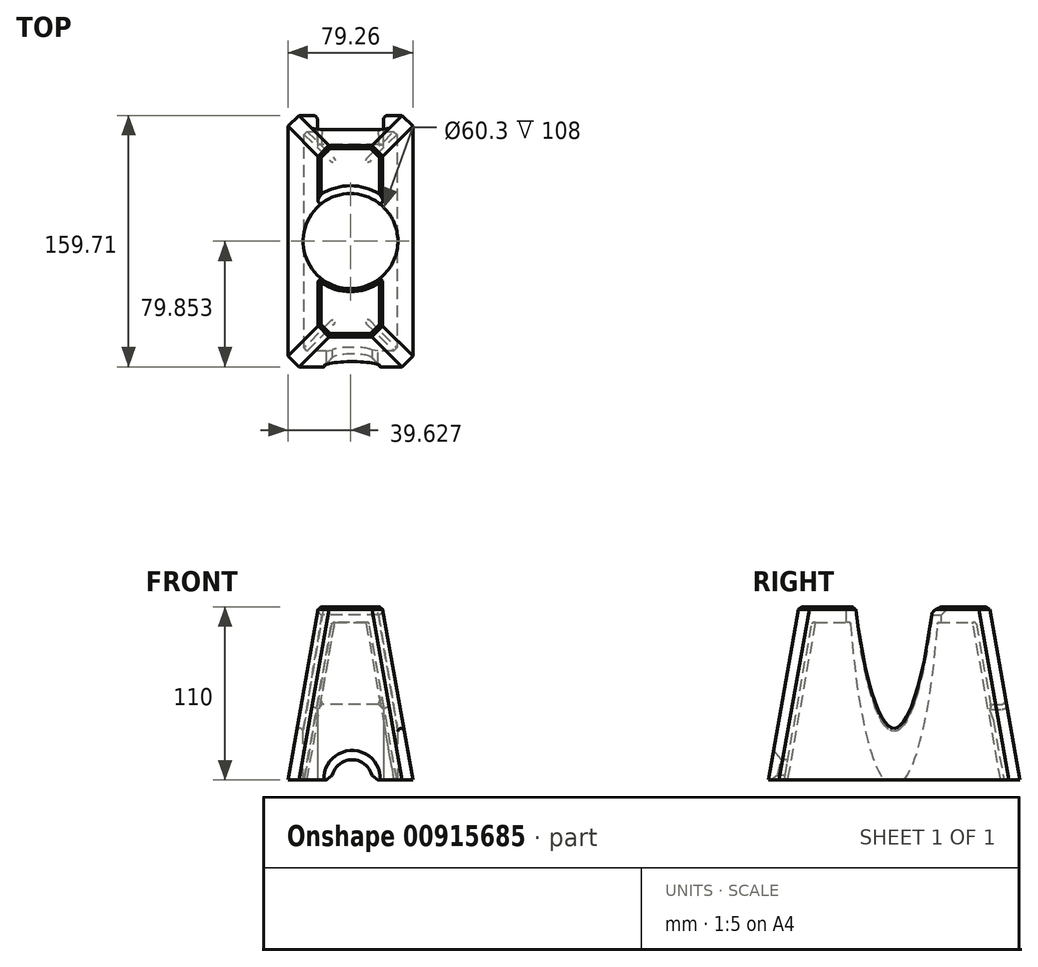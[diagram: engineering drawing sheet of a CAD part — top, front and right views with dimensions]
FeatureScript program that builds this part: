
annotation { "Feature Type Name" : "Feature", "Feature Type Description" : "" }
export const myFeature = defineFeature(function(context is Context, id is Id, definition is map)
    precondition{}
    {
        {
            var Q0;
            Q0=qCreatedBy(makeId("Top.planeOp"),FACE);
            var sketch = newSketch(context, id + "F0", { "sketchPlane" : qUnion([Q0])});
            skLineSegment(sketch, "E0.bottom", {"start": v(58.95, 0) * mm, "end": v(0, 0) * mm});
            skLineSegment(sketch, "E0.top", {"start": v(58.95, 139.4) * mm, "end": v(0, 139.4) * mm});
            skLineSegment(sketch, "E0.left", {"start": v(58.95, 0) * mm, "end": v(58.95, 139.4) * mm});
            skLineSegment(sketch, "E0.right", {"start": v(0, 0) * mm, "end": v(0, 139.4) * mm});
            skSolve(sketch);
        }
        {
            var Q0;
            Q0=makeQuery(id+"F0.imprint","IMPRINT",FACE,{"disambiguationData":[TD([[makeQuery(id+"F0.imprint","IMPRINT",EDGE,{"derivedFrom":sQuery(id+"F0.wireOp",EDGE,"E0.bottom")}),-1.0]])]});
            extrude(context, id + "F1", {"entities" : qUnion([Q0]), "depth" : 100 * mm, "offsetDistance" : 25 * mm, "hasDraft" : true, "draftAngle" : 10 * degree, "draftPullDirection" : true});
        }
        {
            var Q0;
            Q0=makeQuery(id+"F1.opExtrude","CAP_FACE",FACE,{"disambiguationData":[OSD([sQuery(id+"F0.wireOp",EDGE,"E0.bottom"),sQuery(id+"F0.wireOp",EDGE,"E0.top"),sQuery(id+"F0.wireOp",EDGE,"E0.left"),sQuery(id+"F0.wireOp",EDGE,"E0.right")])],"isStart":true});
            shell(context, id + "F2", {"entities" : qUnion([Q0]), "thickness" : 10 * mm, "oppositeDirection" : true});
        }
        {
            var Q0;
            Q0=makeQuery(id+"F1.opExtrude","CAP_FACE",FACE,{"disambiguationData":[OSD([sQuery(id+"F0.wireOp",EDGE,"E0.bottom"),sQuery(id+"F0.wireOp",EDGE,"E0.top"),sQuery(id+"F0.wireOp",EDGE,"E0.left"),sQuery(id+"F0.wireOp",EDGE,"E0.right")])],"isStart":false});
            var sketch = newSketch(context, id + "F3", { "sketchPlane" : qUnion([Q0])});
            skLineSegment(sketch, "E1", {"start": v(29.48, 130.16) * mm, "end": v(29.48, 9.24) * mm});
            skCircle(sketch, "E2", {"center": v(29.48, 69.7) * mm, "radius": 30.15 * mm});
            skSolve(sketch);
        }
        {
            var Q0;
            {var subQ0=sQuery(id+"F3.wireOp",EDGE,"E2");var subQ1=makeQuery(id+"F1.opExtrude","CAP_EDGE",EDGE,{"disambiguationData":[OSD([sQuery(id+"F0.wireOp",EDGE,"E0.left")])],"isStart":false});var subQ2=makeQuery(id+"F3.imprint","INTERSECT",VERTEX,{"disambiguationData":[OD(0.0)],"derivedFrom":[subQ1,subQ0]});Q0=makeQuery(id+"F3.imprint","IMPRINT",FACE,{"disambiguationData":[TD([[makeQuery(id+"F3.imprint","IMPRINT",EDGE,{"disambiguationData":[TD([[subQ2,1.0]])],"derivedFrom":subQ0}),1.0]])]});}
            var Q1;
            {var subQ0=sQuery(id+"F3.wireOp",EDGE,"E2");var subQ1=sQuery(id+"F3.wireOp",EDGE,"E1");var subQ2=makeQuery(id+"F3.imprint","INTERSECT",VERTEX,{"disambiguationData":[OD(0.0)],"derivedFrom":[subQ1,subQ0]});Q1=makeQuery(id+"F3.imprint","IMPRINT",FACE,{"disambiguationData":[TD([[makeQuery(id+"F3.imprint","IMPRINT",EDGE,{"disambiguationData":[TD([[subQ2,-1.0]])],"derivedFrom":subQ1}),1.0]])]});}
            var Q2;
            {var subQ0=sQuery(id+"F3.wireOp",EDGE,"E2");var subQ1=makeQuery(id+"F1.opExtrude","CAP_EDGE",EDGE,{"disambiguationData":[OSD([sQuery(id+"F0.wireOp",EDGE,"E0.right")])],"isStart":false});var subQ2=makeQuery(id+"F3.imprint","INTERSECT",VERTEX,{"disambiguationData":[OD(0.0)],"derivedFrom":[subQ1,subQ0]});Q2=makeQuery(id+"F3.imprint","IMPRINT",FACE,{"disambiguationData":[TD([[makeQuery(id+"F3.imprint","IMPRINT",EDGE,{"disambiguationData":[TD([[subQ2,-1.0]])],"derivedFrom":subQ0}),1.0]])]});}
            var Q3;
            {var subQ0=sQuery(id+"F3.wireOp",EDGE,"E2");var subQ1=sQuery(id+"F3.wireOp",EDGE,"E1");var subQ2=makeQuery(id+"F3.imprint","INTERSECT",VERTEX,{"disambiguationData":[OD(0.0)],"derivedFrom":[subQ1,subQ0]});Q3=makeQuery(id+"F3.imprint","IMPRINT",FACE,{"disambiguationData":[TD([[makeQuery(id+"F3.imprint","IMPRINT",EDGE,{"disambiguationData":[TD([[subQ2,-1.0]])],"derivedFrom":subQ1}),-1.0]])]});}
            var Q4;
            Q4=sQuery(id+"F3.wireOp",EDGE,"E2");
            extrude(context, id + "F4", {"entities" : qUnion([Q0, Q1, Q2, Q3]), "operationType" : NewBodyOperationType.REMOVE, "surfaceEntities" : qUnion([Q4]), "endBound" : BoundingType.THROUGH_ALL, "oppositeDirection" : true, "depth" : 100 * mm, "offsetDistance" : 25 * mm});
        }
        {
            var Q0;
            Q0=makeQuery(id+"F1.opExtrude","CAP_FACE",FACE,{"disambiguationData":[OSD([sQuery(id+"F0.wireOp",EDGE,"E0.bottom"),sQuery(id+"F0.wireOp",EDGE,"E0.top"),sQuery(id+"F0.wireOp",EDGE,"E0.left"),sQuery(id+"F0.wireOp",EDGE,"E0.right")])],"isStart":true});
            var sketch = newSketch(context, id + "F5", { "sketchPlane" : qUnion([Q0])});
            skLineSegment(sketch, "E3", {"start": v(29.48, -149.56) * mm, "end": v(29.48, 10.15) * mm});
            skLineSegment(sketch, "E4.bottom", {"start": v(50.35, -169.76) * mm, "end": v(8.6, -169.76) * mm});
            skLineSegment(sketch, "E4.top", {"start": v(50.35, -129.37) * mm, "end": v(8.6, -129.37) * mm});
            skLineSegment(sketch, "E4.left", {"start": v(50.35, -169.76) * mm, "end": v(50.35, -129.37) * mm});
            skLineSegment(sketch, "E4.right", {"start": v(8.6, -169.76) * mm, "end": v(8.6, -129.37) * mm});
            skPoint(sketch, "E4.middle", {"position": v(29.48, -149.56) * mm});
            skSolve(sketch);
        }
        {
            var Q0;
            {var subQ1=sQuery(id+"F5.wireOp",EDGE,"E4.bottom");Q0=makeQuery(id+"F5.imprint","IMPRINT",FACE,{"disambiguationData":[TD([[makeQuery(id+"F5.imprint","IMPRINT",EDGE,{"derivedFrom":subQ1}),-1.0]])]});}
            var Q1;
            {var subQ0=sQuery(id+"F5.wireOp",EDGE,"E3");var subQ1=sQuery(id+"F0.wireOp",EDGE,"E0.top");var subQ2=makeQuery(id+"F1.opExtrude","CAP_EDGE",EDGE,{"disambiguationData":[OSD([subQ1])],"isStart":true});var subQ3=makeQuery(id+"F5.imprint","INTERSECT",VERTEX,{"derivedFrom":[subQ2,subQ0]});Q1=makeQuery(id+"F5.imprint","IMPRINT",FACE,{"disambiguationData":[TD([[makeQuery(id+"F5.imprint","IMPRINT",EDGE,{"disambiguationData":[TD([[subQ3,-1.0]])],"derivedFrom":subQ2}),-1.0]])]});}
            var Q2;
            {var subQ0=sQuery(id+"F5.wireOp",EDGE,"E3");var subQ1=sQuery(id+"F0.wireOp",EDGE,"E0.top");var subQ2=makeQuery(id+"F1.opExtrude","CAP_EDGE",EDGE,{"disambiguationData":[OSD([subQ1])],"isStart":true});var subQ3=makeQuery(id+"F5.imprint","INTERSECT",VERTEX,{"derivedFrom":[subQ2,subQ0]});Q2=makeQuery(id+"F5.imprint","IMPRINT",FACE,{"disambiguationData":[TD([[makeQuery(id+"F5.imprint","IMPRINT",EDGE,{"disambiguationData":[TD([[subQ3,1.0]])],"derivedFrom":subQ2}),-1.0]])]});}
            var Q3;
            {var subQ0=sQuery(id+"F5.wireOp",EDGE,"E4.top");var subQ6=sQuery(id+"F5.wireOp",EDGE,"E4.left");var subQ8=makeQuery(id+"F5.imprint","INTERSECT",VERTEX,{"derivedFrom":[subQ0,subQ6]});Q3=makeQuery(id+"F5.imprint","IMPRINT",FACE,{"disambiguationData":[TD([[makeQuery(id+"F5.imprint","IMPRINT",EDGE,{"disambiguationData":[TD([[subQ8,-1.0]])],"derivedFrom":subQ0}),1.0]])]});}
            var Q4;
            {var subQ0=sQuery(id+"F5.wireOp",EDGE,"E4.top");var subQ6=sQuery(id+"F5.wireOp",EDGE,"E4.right");var subQ7=makeQuery(id+"F5.imprint","INTERSECT",VERTEX,{"derivedFrom":[subQ0,subQ6]});Q4=makeQuery(id+"F5.imprint","IMPRINT",FACE,{"disambiguationData":[TD([[makeQuery(id+"F5.imprint","IMPRINT",EDGE,{"disambiguationData":[TD([[subQ7,1.0]])],"derivedFrom":subQ0}),1.0]])]});}
            extrude(context, id + "F6", {"entities" : qUnion([Q0, Q1, Q2, Q3, Q4]), "operationType" : NewBodyOperationType.REMOVE, "oppositeDirection" : true, "depth" : 48 * mm, "offsetDistance" : 25 * mm});
        }
        {
            var Q0;
            Q0=qCreatedBy(makeId("Front.planeOp"),FACE);
            var sketch = newSketch(context, id + "F7", { "sketchPlane" : qUnion([Q0])});
            skCircle(sketch, "E5", {"center": v(30.53, 0) * mm, "radius": 12.96 * mm});
            skSolve(sketch);
        }
        {
            var Q0;
            Q0=makeQuery(id+"F7.imprint","IMPRINT",FACE,{"disambiguationData":[TD([[makeQuery(id+"F7.imprint","IMPRINT",EDGE,{"derivedFrom":sQuery(id+"F7.wireOp",EDGE,"E5")}),1.0]])]});
            var Q1;
            Q1=sQuery(id+"F7.wireOp",EDGE,"E5");
            extrude(context, id + "F8", {"entities" : qUnion([Q0]), "operationType" : NewBodyOperationType.REMOVE, "surfaceEntities" : qUnion([Q1]), "endBound" : BoundingType.SYMMETRIC, "oppositeDirection" : true, "depth" : 100 * mm, "offsetDistance" : 25 * mm});
        }
        {
            var Q0;
            Q0=makeQuery(id+"F4.boolean.opBoolean","COPY",EDGE,{"disambiguationData":[OD(0.0)],"derivedFrom":makeQuery(id+"F4.opExtrude","CAP_EDGE",EDGE,{"disambiguationData":[OSD([sQuery(id+"F3.wireOp",EDGE,"E2")])],"isStart":true})});
            var Q1;
            Q1=makeQuery(id+"F4.boolean.opBoolean","COPY",EDGE,{"disambiguationData":[OD(1.0)],"derivedFrom":makeQuery(id+"F4.opExtrude","CAP_EDGE",EDGE,{"disambiguationData":[OSD([sQuery(id+"F3.wireOp",EDGE,"E2")])],"isStart":true})});
            chamfer(context, id + "F9", {"entities" : qUnion([Q0, Q1]), "width" : 5 * mm, "tangentPropagation" : true});
        }
        {
            var Q0;
            Q0=makeQuery(id+"F4.boolean.opBoolean","INTERSECT",EDGE,{"derivedFrom":[makeQuery(id+"F1.opExtrude","SWEPT_FACE",FACE,{"disambiguationData":[OSD([sQuery(id+"F0.wireOp",EDGE,"E0.right")])]}),makeQuery(id+"F4.opExtrude","SWEPT_FACE",FACE,{"disambiguationData":[OSD([sQuery(id+"F3.wireOp",EDGE,"E2")])]})]});
            var Q1;
            Q1=makeQuery(id+"F4.boolean.opBoolean","INTERSECT",EDGE,{"derivedFrom":[makeQuery(id+"F1.opExtrude","SWEPT_FACE",FACE,{"disambiguationData":[OSD([sQuery(id+"F0.wireOp",EDGE,"E0.left")])]}),makeQuery(id+"F4.opExtrude","SWEPT_FACE",FACE,{"disambiguationData":[OSD([sQuery(id+"F3.wireOp",EDGE,"E2")])]})]});
            fillet(context, id + "F10", {"entities" : qUnion([Q0, Q1]), "radius" : 2 * mm, "tangentPropagation" : true, "allowEdgeOverflow" : false});
        }
        {
            var Q0;
            Q0=makeQuery(id+"F6.boolean.opBoolean","COPY",EDGE,{"derivedFrom":makeQuery(id+"F6.opExtrude","CAP_EDGE",EDGE,{"disambiguationData":[OSD([sQuery(id+"F5.wireOp",EDGE,"E4.left")])],"isStart":false})});
            var Q1;
            Q1=makeQuery(id+"F6.boolean.opBoolean","COPY",EDGE,{"derivedFrom":makeQuery(id+"F6.opExtrude","CAP_EDGE",EDGE,{"disambiguationData":[OSD([sQuery(id+"F5.wireOp",EDGE,"E4.right")])],"isStart":false})});
            chamfer(context, id + "F11", {"entities" : qUnion([Q0, Q1]), "width" : 3 * mm, "tangentPropagation" : true});
        }
        {
            var Q0;
            Q0=makeQuery(id+"F8.boolean.opBoolean","INTERSECT",EDGE,{"disambiguationData":[OD(1.0)],"derivedFrom":[makeQuery(id+"F1.opExtrude","CAP_FACE",FACE,{"disambiguationData":[OSD([sQuery(id+"F0.wireOp",EDGE,"E0.bottom"),sQuery(id+"F0.wireOp",EDGE,"E0.top"),sQuery(id+"F0.wireOp",EDGE,"E0.left"),sQuery(id+"F0.wireOp",EDGE,"E0.right")])],"isStart":true}),makeQuery(id+"F8.opExtrude","SWEPT_FACE",FACE,{"disambiguationData":[OSD([sQuery(id+"F7.wireOp",EDGE,"E5")])]})]});
            var Q1;
            Q1=makeQuery(id+"F8.boolean.opBoolean","INTERSECT",EDGE,{"disambiguationData":[OD(0.0)],"derivedFrom":[makeQuery(id+"F1.opExtrude","CAP_FACE",FACE,{"disambiguationData":[OSD([sQuery(id+"F0.wireOp",EDGE,"E0.bottom"),sQuery(id+"F0.wireOp",EDGE,"E0.top"),sQuery(id+"F0.wireOp",EDGE,"E0.left"),sQuery(id+"F0.wireOp",EDGE,"E0.right")])],"isStart":true}),makeQuery(id+"F8.opExtrude","SWEPT_FACE",FACE,{"disambiguationData":[OSD([sQuery(id+"F7.wireOp",EDGE,"E5")])]})]});
            chamfer(context, id + "F12", {"entities" : qUnion([Q0, Q1]), "width" : 4 * mm, "tangentPropagation" : true});
        }
        {
            var Q0;
            Q0=makeQuery(id+"F2.opShell","OFFSET_EDGE",EDGE,{"disambiguationData":[OSD([sQuery(id+"F0.wireOp",EDGE,"E0.bottom"),sQuery(id+"F0.wireOp",EDGE,"E0.right")])]});
            var Q1;
            Q1=makeQuery(id+"F2.opShell","OFFSET_EDGE",EDGE,{"disambiguationData":[OSD([sQuery(id+"F0.wireOp",EDGE,"E0.bottom"),sQuery(id+"F0.wireOp",EDGE,"E0.left")])]});
            var Q2;
            Q2=makeQuery(id+"F2.opShell","OFFSET_EDGE",EDGE,{"disambiguationData":[OSD([sQuery(id+"F0.wireOp",EDGE,"E0.top"),sQuery(id+"F0.wireOp",EDGE,"E0.left")])]});
            var Q3;
            Q3=makeQuery(id+"F2.opShell","OFFSET_EDGE",EDGE,{"disambiguationData":[OSD([sQuery(id+"F0.wireOp",EDGE,"E0.top"),sQuery(id+"F0.wireOp",EDGE,"E0.right")])]});
            chamfer(context, id + "F13", {"entities" : qUnion([Q0, Q1, Q2, Q3]), "width" : 2 * mm, "tangentPropagation" : true});
        }
        {
            var Q0;
            Q0=makeQuery(id+"F1.opExtrude","SWEPT_EDGE",EDGE,{"disambiguationData":[OSD([sQuery(id+"F0.wireOp",EDGE,"E0.bottom"),sQuery(id+"F0.wireOp",EDGE,"E0.right")])]});
            var Q1;
            Q1=makeQuery(id+"F1.opExtrude","SWEPT_EDGE",EDGE,{"disambiguationData":[OSD([sQuery(id+"F0.wireOp",EDGE,"E0.bottom"),sQuery(id+"F0.wireOp",EDGE,"E0.left")])]});
            var Q2;
            Q2=makeQuery(id+"F1.opExtrude","SWEPT_EDGE",EDGE,{"disambiguationData":[OSD([sQuery(id+"F0.wireOp",EDGE,"E0.top"),sQuery(id+"F0.wireOp",EDGE,"E0.right")])]});
            var Q3;
            Q3=makeQuery(id+"F1.opExtrude","SWEPT_EDGE",EDGE,{"disambiguationData":[OSD([sQuery(id+"F0.wireOp",EDGE,"E0.top"),sQuery(id+"F0.wireOp",EDGE,"E0.left")])]});
            chamfer(context, id + "F14", {"entities" : qUnion([Q0, Q1, Q2, Q3]), "width" : 7 * mm, "tangentPropagation" : true});
        }
        {
            var Q0;
            {var subQ0=sQuery(id+"F0.wireOp",EDGE,"E0.left");var subQ1=sQuery(id+"F0.wireOp",EDGE,"E0.top");Q0=makeQuery(id+"F4.boolean.opBoolean","SPLIT",EDGE,{"disambiguationData":[TD([makeQuery(id+"F2.opShell","OFFSET_FACE",FACE,{"disambiguationData":[OSD([subQ1])]})])],"derivedFrom":makeQuery(id+"F2.opShell","OFFSET_EDGE",EDGE,{"disambiguationData":[OSD([subQ0]),TDD([makeQuery(id+"F1.opExtrude","CAP_EDGE",EDGE,{"disambiguationData":[OSD([subQ0])],"isStart":false})])]})});}
            var Q1;
            {var subQ0=sQuery(id+"F0.wireOp",EDGE,"E0.top");var subQ1=sQuery(id+"F0.wireOp",EDGE,"E0.left");var subQ2=sQuery(id+"F0.wireOp",EDGE,"E0.right");Q1=makeQuery(id+"F13.opChamfer","BLEND_EDGE",EDGE,{"blendedFrom":[makeQuery(id+"F2.opShell","OFFSET_EDGE",EDGE,{"disambiguationData":[OSD([subQ0,subQ1])]}),makeQuery(id+"F4.boolean.opBoolean","SPLIT",FACE,{"disambiguationData":[TD([makeQuery(id+"F2.opShell","OFFSET_FACE",FACE,{"disambiguationData":[OSD([subQ0])]})])],"derivedFrom":makeQuery(id+"F2.opShell","OFFSET_FACE",FACE,{"disambiguationData":[OSD([sQuery(id+"F0.wireOp",EDGE,"E0.bottom"),subQ0,subQ1,subQ2])]})})],"blendedInto":[makeQuery(id+"F4.boolean.opBoolean","SPLIT",FACE,{"disambiguationData":[TD([makeQuery(id+"F2.opShell","OFFSET_FACE",FACE,{"disambiguationData":[OSD([subQ0])]})])],"derivedFrom":makeQuery(id+"F2.opShell","OFFSET_FACE",FACE,{"disambiguationData":[OSD([sQuery(id+"F0.wireOp",EDGE,"E0.bottom"),subQ0,subQ1,subQ2])]})})]});}
            var Q2;
            {var subQ0=sQuery(id+"F0.wireOp",EDGE,"E0.top");Q2=makeQuery(id+"F2.opShell","OFFSET_EDGE",EDGE,{"disambiguationData":[OSD([subQ0]),TDD([makeQuery(id+"F1.opExtrude","CAP_EDGE",EDGE,{"disambiguationData":[OSD([subQ0])],"isStart":false})])]});}
            var Q3;
            {var subQ0=sQuery(id+"F0.wireOp",EDGE,"E0.top");var subQ1=sQuery(id+"F0.wireOp",EDGE,"E0.left");var subQ2=sQuery(id+"F0.wireOp",EDGE,"E0.right");Q3=makeQuery(id+"F13.opChamfer","BLEND_EDGE",EDGE,{"blendedFrom":[makeQuery(id+"F2.opShell","OFFSET_EDGE",EDGE,{"disambiguationData":[OSD([subQ0,subQ2])]}),makeQuery(id+"F4.boolean.opBoolean","SPLIT",FACE,{"disambiguationData":[TD([makeQuery(id+"F2.opShell","OFFSET_FACE",FACE,{"disambiguationData":[OSD([subQ0])]})])],"derivedFrom":makeQuery(id+"F2.opShell","OFFSET_FACE",FACE,{"disambiguationData":[OSD([sQuery(id+"F0.wireOp",EDGE,"E0.bottom"),subQ0,subQ1,subQ2])]})})],"blendedInto":[makeQuery(id+"F4.boolean.opBoolean","SPLIT",FACE,{"disambiguationData":[TD([makeQuery(id+"F2.opShell","OFFSET_FACE",FACE,{"disambiguationData":[OSD([subQ0])]})])],"derivedFrom":makeQuery(id+"F2.opShell","OFFSET_FACE",FACE,{"disambiguationData":[OSD([sQuery(id+"F0.wireOp",EDGE,"E0.bottom"),subQ0,subQ1,subQ2])]})})]});}
            var Q4;
            {var subQ0=sQuery(id+"F0.wireOp",EDGE,"E0.right");var subQ1=sQuery(id+"F0.wireOp",EDGE,"E0.top");Q4=makeQuery(id+"F4.boolean.opBoolean","SPLIT",EDGE,{"disambiguationData":[TD([makeQuery(id+"F2.opShell","OFFSET_FACE",FACE,{"disambiguationData":[OSD([subQ1])]})])],"derivedFrom":makeQuery(id+"F2.opShell","OFFSET_EDGE",EDGE,{"disambiguationData":[OSD([subQ0]),TDD([makeQuery(id+"F1.opExtrude","CAP_EDGE",EDGE,{"disambiguationData":[OSD([subQ0])],"isStart":false})])]})});}
            var Q5;
            {var subQ0=sQuery(id+"F0.wireOp",EDGE,"E0.left");var subQ1=sQuery(id+"F0.wireOp",EDGE,"E0.bottom");Q5=makeQuery(id+"F4.boolean.opBoolean","SPLIT",EDGE,{"disambiguationData":[TD([makeQuery(id+"F2.opShell","OFFSET_FACE",FACE,{"disambiguationData":[OSD([subQ1])]})])],"derivedFrom":makeQuery(id+"F2.opShell","OFFSET_EDGE",EDGE,{"disambiguationData":[OSD([subQ0]),TDD([makeQuery(id+"F1.opExtrude","CAP_EDGE",EDGE,{"disambiguationData":[OSD([subQ0])],"isStart":false})])]})});}
            var Q6;
            {var subQ0=sQuery(id+"F0.wireOp",EDGE,"E0.bottom");var subQ1=sQuery(id+"F0.wireOp",EDGE,"E0.left");var subQ2=sQuery(id+"F0.wireOp",EDGE,"E0.right");Q6=makeQuery(id+"F13.opChamfer","BLEND_EDGE",EDGE,{"blendedFrom":[makeQuery(id+"F2.opShell","OFFSET_EDGE",EDGE,{"disambiguationData":[OSD([subQ0,subQ1])]}),makeQuery(id+"F4.boolean.opBoolean","SPLIT",FACE,{"disambiguationData":[TD([makeQuery(id+"F2.opShell","OFFSET_FACE",FACE,{"disambiguationData":[OSD([subQ0])]})])],"derivedFrom":makeQuery(id+"F2.opShell","OFFSET_FACE",FACE,{"disambiguationData":[OSD([subQ0,sQuery(id+"F0.wireOp",EDGE,"E0.top"),subQ1,subQ2])]})})],"blendedInto":[makeQuery(id+"F4.boolean.opBoolean","SPLIT",FACE,{"disambiguationData":[TD([makeQuery(id+"F2.opShell","OFFSET_FACE",FACE,{"disambiguationData":[OSD([subQ0])]})])],"derivedFrom":makeQuery(id+"F2.opShell","OFFSET_FACE",FACE,{"disambiguationData":[OSD([subQ0,sQuery(id+"F0.wireOp",EDGE,"E0.top"),subQ1,subQ2])]})})]});}
            var Q7;
            {var subQ0=sQuery(id+"F0.wireOp",EDGE,"E0.bottom");Q7=makeQuery(id+"F2.opShell","OFFSET_EDGE",EDGE,{"disambiguationData":[OSD([subQ0]),TDD([makeQuery(id+"F1.opExtrude","CAP_EDGE",EDGE,{"disambiguationData":[OSD([subQ0])],"isStart":false})])]});}
            var Q8;
            {var subQ0=sQuery(id+"F0.wireOp",EDGE,"E0.right");var subQ1=sQuery(id+"F0.wireOp",EDGE,"E0.bottom");Q8=makeQuery(id+"F4.boolean.opBoolean","SPLIT",EDGE,{"disambiguationData":[TD([makeQuery(id+"F2.opShell","OFFSET_FACE",FACE,{"disambiguationData":[OSD([subQ1])]})])],"derivedFrom":makeQuery(id+"F2.opShell","OFFSET_EDGE",EDGE,{"disambiguationData":[OSD([subQ0]),TDD([makeQuery(id+"F1.opExtrude","CAP_EDGE",EDGE,{"disambiguationData":[OSD([subQ0])],"isStart":false})])]})});}
            var Q9;
            {var subQ0=sQuery(id+"F0.wireOp",EDGE,"E0.bottom");var subQ1=sQuery(id+"F0.wireOp",EDGE,"E0.left");var subQ2=sQuery(id+"F0.wireOp",EDGE,"E0.right");Q9=makeQuery(id+"F13.opChamfer","BLEND_EDGE",EDGE,{"blendedFrom":[makeQuery(id+"F2.opShell","OFFSET_EDGE",EDGE,{"disambiguationData":[OSD([subQ0,subQ2])]}),makeQuery(id+"F4.boolean.opBoolean","SPLIT",FACE,{"disambiguationData":[TD([makeQuery(id+"F2.opShell","OFFSET_FACE",FACE,{"disambiguationData":[OSD([subQ0])]})])],"derivedFrom":makeQuery(id+"F2.opShell","OFFSET_FACE",FACE,{"disambiguationData":[OSD([subQ0,sQuery(id+"F0.wireOp",EDGE,"E0.top"),subQ1,subQ2])]})})],"blendedInto":[makeQuery(id+"F4.boolean.opBoolean","SPLIT",FACE,{"disambiguationData":[TD([makeQuery(id+"F2.opShell","OFFSET_FACE",FACE,{"disambiguationData":[OSD([subQ0])]})])],"derivedFrom":makeQuery(id+"F2.opShell","OFFSET_FACE",FACE,{"disambiguationData":[OSD([subQ0,sQuery(id+"F0.wireOp",EDGE,"E0.top"),subQ1,subQ2])]})})]});}
            fillet(context, id + "F15", {"entities" : qUnion([Q0, Q1, Q2, Q3, Q4, Q5, Q6, Q7, Q8, Q9]), "radius" : 1 * mm, "tangentPropagation" : true, "allowEdgeOverflow" : false});
        }
        {
            var Q0;
            Q0=makeQuery(id+"F8.boolean.opBoolean","INTERSECT",EDGE,{"derivedFrom":[makeQuery(id+"F1.opExtrude","SWEPT_FACE",FACE,{"disambiguationData":[OSD([sQuery(id+"F0.wireOp",EDGE,"E0.bottom")])]}),makeQuery(id+"F8.opExtrude","SWEPT_FACE",FACE,{"disambiguationData":[OSD([sQuery(id+"F7.wireOp",EDGE,"E5")])]})]});
            chamfer(context, id + "F16", {"entities" : qUnion([Q0]), "width" : 5 * mm, "tangentPropagation" : true});
        }
        {
            var Q0;
            Q0=makeQuery(id+"F6.boolean.opBoolean","INTERSECT",EDGE,{"derivedFrom":[makeQuery(id+"F1.opExtrude","SWEPT_FACE",FACE,{"disambiguationData":[OSD([sQuery(id+"F0.wireOp",EDGE,"E0.top")])]}),makeQuery(id+"F6.opExtrude","SWEPT_FACE",FACE,{"disambiguationData":[OSD([sQuery(id+"F5.wireOp",EDGE,"E4.left")])]})]});
            var Q1;
            Q1=makeQuery(id+"F6.boolean.opBoolean","INTERSECT",EDGE,{"derivedFrom":[makeQuery(id+"F1.opExtrude","SWEPT_FACE",FACE,{"disambiguationData":[OSD([sQuery(id+"F0.wireOp",EDGE,"E0.top")])]}),makeQuery(id+"F6.opExtrude","SWEPT_FACE",FACE,{"disambiguationData":[OSD([sQuery(id+"F5.wireOp",EDGE,"E4.right")])]})]});
            var Q2;
            Q2=makeQuery(id+"F11.opChamfer","BLEND_EDGE",EDGE,{"blendedFrom":[makeQuery(id+"F6.boolean.opBoolean","COPY",EDGE,{"derivedFrom":makeQuery(id+"F6.opExtrude","CAP_EDGE",EDGE,{"disambiguationData":[OSD([sQuery(id+"F5.wireOp",EDGE,"E4.left")])],"isStart":false})}),makeQuery(id+"F1.opExtrude","SWEPT_FACE",FACE,{"disambiguationData":[OSD([sQuery(id+"F0.wireOp",EDGE,"E0.top")])]})],"blendedInto":[makeQuery(id+"F1.opExtrude","SWEPT_FACE",FACE,{"disambiguationData":[OSD([sQuery(id+"F0.wireOp",EDGE,"E0.top")])]})]});
            var Q3;
            Q3=makeQuery(id+"F6.boolean.opBoolean","INTERSECT",EDGE,{"derivedFrom":[makeQuery(id+"F1.opExtrude","SWEPT_FACE",FACE,{"disambiguationData":[OSD([sQuery(id+"F0.wireOp",EDGE,"E0.top")])]}),makeQuery(id+"F6.opExtrude","CAP_FACE",FACE,{"disambiguationData":[OSD([sQuery(id+"F5.wireOp",EDGE,"E4.bottom"),sQuery(id+"F5.wireOp",EDGE,"E4.top"),sQuery(id+"F5.wireOp",EDGE,"E4.left"),sQuery(id+"F5.wireOp",EDGE,"E4.right")])],"isStart":false})]});
            var Q4;
            Q4=makeQuery(id+"F11.opChamfer","BLEND_EDGE",EDGE,{"blendedFrom":[makeQuery(id+"F6.boolean.opBoolean","COPY",EDGE,{"derivedFrom":makeQuery(id+"F6.opExtrude","CAP_EDGE",EDGE,{"disambiguationData":[OSD([sQuery(id+"F5.wireOp",EDGE,"E4.right")])],"isStart":false})}),makeQuery(id+"F1.opExtrude","SWEPT_FACE",FACE,{"disambiguationData":[OSD([sQuery(id+"F0.wireOp",EDGE,"E0.top")])]})],"blendedInto":[makeQuery(id+"F1.opExtrude","SWEPT_FACE",FACE,{"disambiguationData":[OSD([sQuery(id+"F0.wireOp",EDGE,"E0.top")])]})]});
            fillet(context, id + "F17", {"entities" : qUnion([Q0, Q1, Q2, Q3, Q4]), "radius" : 3 * mm, "tangentPropagation" : true, "allowEdgeOverflow" : false});
        }
        {
            var Q0;
            {var subQ0=sQuery(id+"F0.wireOp",EDGE,"E0.bottom");var subQ1=sQuery(id+"F0.wireOp",EDGE,"E0.left");Q0=makeQuery(id+"F4.boolean.opBoolean","SPLIT",EDGE,{"disambiguationData":[TD([makeQuery(id+"F1.opExtrude","SWEPT_FACE",FACE,{"disambiguationData":[OSD([subQ0])]})])],"derivedFrom":makeQuery(id+"F1.opExtrude","CAP_EDGE",EDGE,{"disambiguationData":[OSD([subQ1])],"isStart":false})});}
            var Q1;
            {var subQ0=sQuery(id+"F0.wireOp",EDGE,"E0.bottom");var subQ1=sQuery(id+"F0.wireOp",EDGE,"E0.right");var subQ2=sQuery(id+"F0.wireOp",EDGE,"E0.left");Q1=makeQuery(id+"F14.opChamfer","BLEND_EDGE",EDGE,{"blendedFrom":[makeQuery(id+"F1.opExtrude","SWEPT_EDGE",EDGE,{"disambiguationData":[OSD([subQ0,subQ2])]}),makeQuery(id+"F4.boolean.opBoolean","SPLIT",FACE,{"disambiguationData":[TD([makeQuery(id+"F1.opExtrude","SWEPT_FACE",FACE,{"disambiguationData":[OSD([subQ0])]})])],"derivedFrom":makeQuery(id+"F1.opExtrude","CAP_FACE",FACE,{"disambiguationData":[OSD([subQ0,sQuery(id+"F0.wireOp",EDGE,"E0.top"),subQ2,subQ1])],"isStart":false})})],"blendedInto":[makeQuery(id+"F4.boolean.opBoolean","SPLIT",FACE,{"disambiguationData":[TD([makeQuery(id+"F1.opExtrude","SWEPT_FACE",FACE,{"disambiguationData":[OSD([subQ0])]})])],"derivedFrom":makeQuery(id+"F1.opExtrude","CAP_FACE",FACE,{"disambiguationData":[OSD([subQ0,sQuery(id+"F0.wireOp",EDGE,"E0.top"),subQ2,subQ1])],"isStart":false})})]});}
            var Q2;
            Q2=makeQuery(id+"F1.opExtrude","CAP_EDGE",EDGE,{"disambiguationData":[OSD([sQuery(id+"F0.wireOp",EDGE,"E0.bottom")])],"isStart":false});
            var Q3;
            {var subQ0=sQuery(id+"F0.wireOp",EDGE,"E0.bottom");var subQ1=sQuery(id+"F0.wireOp",EDGE,"E0.right");var subQ2=sQuery(id+"F0.wireOp",EDGE,"E0.left");Q3=makeQuery(id+"F14.opChamfer","BLEND_EDGE",EDGE,{"blendedFrom":[makeQuery(id+"F1.opExtrude","SWEPT_EDGE",EDGE,{"disambiguationData":[OSD([subQ0,subQ1])]}),makeQuery(id+"F4.boolean.opBoolean","SPLIT",FACE,{"disambiguationData":[TD([makeQuery(id+"F1.opExtrude","SWEPT_FACE",FACE,{"disambiguationData":[OSD([subQ0])]})])],"derivedFrom":makeQuery(id+"F1.opExtrude","CAP_FACE",FACE,{"disambiguationData":[OSD([subQ0,sQuery(id+"F0.wireOp",EDGE,"E0.top"),subQ2,subQ1])],"isStart":false})})],"blendedInto":[makeQuery(id+"F4.boolean.opBoolean","SPLIT",FACE,{"disambiguationData":[TD([makeQuery(id+"F1.opExtrude","SWEPT_FACE",FACE,{"disambiguationData":[OSD([subQ0])]})])],"derivedFrom":makeQuery(id+"F1.opExtrude","CAP_FACE",FACE,{"disambiguationData":[OSD([subQ0,sQuery(id+"F0.wireOp",EDGE,"E0.top"),subQ2,subQ1])],"isStart":false})})]});}
            var Q4;
            {var subQ0=sQuery(id+"F0.wireOp",EDGE,"E0.bottom");var subQ1=sQuery(id+"F0.wireOp",EDGE,"E0.right");Q4=makeQuery(id+"F4.boolean.opBoolean","SPLIT",EDGE,{"disambiguationData":[TD([makeQuery(id+"F1.opExtrude","SWEPT_FACE",FACE,{"disambiguationData":[OSD([subQ0])]})])],"derivedFrom":makeQuery(id+"F1.opExtrude","CAP_EDGE",EDGE,{"disambiguationData":[OSD([subQ1])],"isStart":false})});}
            var Q5;
            {var subQ0=sQuery(id+"F0.wireOp",EDGE,"E0.right");var subQ1=sQuery(id+"F0.wireOp",EDGE,"E0.top");Q5=makeQuery(id+"F4.boolean.opBoolean","SPLIT",EDGE,{"disambiguationData":[TD([makeQuery(id+"F1.opExtrude","SWEPT_FACE",FACE,{"disambiguationData":[OSD([subQ1])]})])],"derivedFrom":makeQuery(id+"F1.opExtrude","CAP_EDGE",EDGE,{"disambiguationData":[OSD([subQ0])],"isStart":false})});}
            var Q6;
            {var subQ0=sQuery(id+"F0.wireOp",EDGE,"E0.top");var subQ1=sQuery(id+"F0.wireOp",EDGE,"E0.left");var subQ2=sQuery(id+"F0.wireOp",EDGE,"E0.right");Q6=makeQuery(id+"F14.opChamfer","BLEND_EDGE",EDGE,{"blendedFrom":[makeQuery(id+"F1.opExtrude","SWEPT_EDGE",EDGE,{"disambiguationData":[OSD([subQ0,subQ2])]}),makeQuery(id+"F4.boolean.opBoolean","SPLIT",FACE,{"disambiguationData":[TD([makeQuery(id+"F1.opExtrude","SWEPT_FACE",FACE,{"disambiguationData":[OSD([subQ0])]})])],"derivedFrom":makeQuery(id+"F1.opExtrude","CAP_FACE",FACE,{"disambiguationData":[OSD([sQuery(id+"F0.wireOp",EDGE,"E0.bottom"),subQ0,subQ1,subQ2])],"isStart":false})})],"blendedInto":[makeQuery(id+"F4.boolean.opBoolean","SPLIT",FACE,{"disambiguationData":[TD([makeQuery(id+"F1.opExtrude","SWEPT_FACE",FACE,{"disambiguationData":[OSD([subQ0])]})])],"derivedFrom":makeQuery(id+"F1.opExtrude","CAP_FACE",FACE,{"disambiguationData":[OSD([sQuery(id+"F0.wireOp",EDGE,"E0.bottom"),subQ0,subQ1,subQ2])],"isStart":false})})]});}
            var Q7;
            Q7=makeQuery(id+"F1.opExtrude","CAP_EDGE",EDGE,{"disambiguationData":[OSD([sQuery(id+"F0.wireOp",EDGE,"E0.top")])],"isStart":false});
            var Q8;
            {var subQ0=sQuery(id+"F0.wireOp",EDGE,"E0.top");var subQ1=sQuery(id+"F0.wireOp",EDGE,"E0.left");var subQ2=sQuery(id+"F0.wireOp",EDGE,"E0.right");Q8=makeQuery(id+"F14.opChamfer","BLEND_EDGE",EDGE,{"blendedFrom":[makeQuery(id+"F1.opExtrude","SWEPT_EDGE",EDGE,{"disambiguationData":[OSD([subQ0,subQ1])]}),makeQuery(id+"F4.boolean.opBoolean","SPLIT",FACE,{"disambiguationData":[TD([makeQuery(id+"F1.opExtrude","SWEPT_FACE",FACE,{"disambiguationData":[OSD([subQ0])]})])],"derivedFrom":makeQuery(id+"F1.opExtrude","CAP_FACE",FACE,{"disambiguationData":[OSD([sQuery(id+"F0.wireOp",EDGE,"E0.bottom"),subQ0,subQ1,subQ2])],"isStart":false})})],"blendedInto":[makeQuery(id+"F4.boolean.opBoolean","SPLIT",FACE,{"disambiguationData":[TD([makeQuery(id+"F1.opExtrude","SWEPT_FACE",FACE,{"disambiguationData":[OSD([subQ0])]})])],"derivedFrom":makeQuery(id+"F1.opExtrude","CAP_FACE",FACE,{"disambiguationData":[OSD([sQuery(id+"F0.wireOp",EDGE,"E0.bottom"),subQ0,subQ1,subQ2])],"isStart":false})})]});}
            var Q9;
            {var subQ0=sQuery(id+"F0.wireOp",EDGE,"E0.left");var subQ1=sQuery(id+"F0.wireOp",EDGE,"E0.top");Q9=makeQuery(id+"F4.boolean.opBoolean","SPLIT",EDGE,{"disambiguationData":[TD([makeQuery(id+"F1.opExtrude","SWEPT_FACE",FACE,{"disambiguationData":[OSD([subQ1])]})])],"derivedFrom":makeQuery(id+"F1.opExtrude","CAP_EDGE",EDGE,{"disambiguationData":[OSD([subQ0])],"isStart":false})});}
            chamfer(context, id + "F18", {"entities" : qUnion([Q0, Q1, Q2, Q3, Q4, Q5, Q6, Q7, Q8, Q9]), "width" : 2 * mm, "tangentPropagation" : true});
        }
    });
